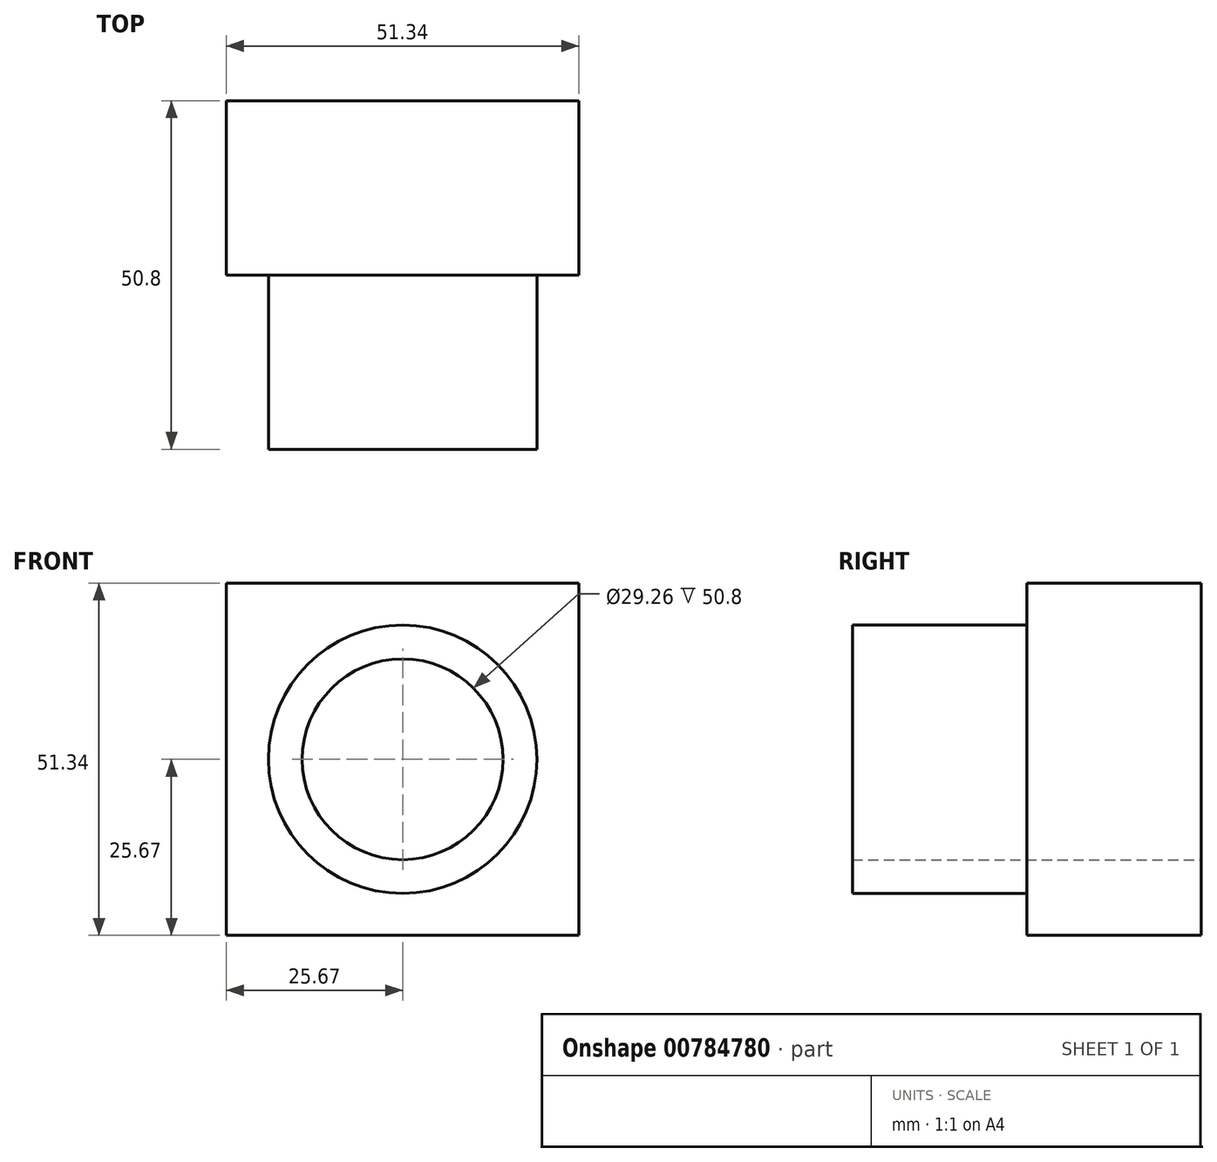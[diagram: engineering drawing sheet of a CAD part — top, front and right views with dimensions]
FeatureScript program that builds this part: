
annotation { "Feature Type Name" : "Feature", "Feature Type Description" : "" }
export const myFeature = defineFeature(function(context is Context, id is Id, definition is map)
    precondition{}
    {
        {
            var Q0;
            Q0=qCreatedBy(makeId("Front.planeOp"),FACE);
            var sketch = newSketch(context, id + "F0", { "sketchPlane" : qUnion([Q0])});
            skLineSegment(sketch, "E0.bottom", {"start": v(-25.67, -25.67) * mm, "end": v(25.67, -25.67) * mm});
            skLineSegment(sketch, "E0.top", {"start": v(-25.67, 25.67) * mm, "end": v(25.67, 25.67) * mm});
            skLineSegment(sketch, "E0.left", {"start": v(-25.67, -25.67) * mm, "end": v(-25.67, 25.67) * mm});
            skLineSegment(sketch, "E0.right", {"start": v(25.67, -25.67) * mm, "end": v(25.67, 25.67) * mm});
            skCircle(sketch, "E1", {"center": v(0, 0) * mm, "radius": 19.56 * mm});
            skCircle(sketch, "E2", {"center": v(0, 0) * mm, "radius": 14.63 * mm});
            skSolve(sketch);
        }
        {
            var Q0;
            Q0 = qSketchRegion(id + "F0", true);
            extrude(context, id + "F1", {"entities" : qUnion([Q0]), "depth" : 25.4 * mm, "offsetDistance" : 25.4 * mm});
        }
        {
            var Q0;
            Q0=makeQuery(id+"F0.imprint","IMPRINT",FACE,{"disambiguationData":[TD([[makeQuery(id+"F0.imprint","IMPRINT",EDGE,{"derivedFrom":sQuery(id+"F0.wireOp",EDGE,"E1")}),1.0]])]});
            extrude(context, id + "F2", {"entities" : qUnion([Q0]), "operationType" : NewBodyOperationType.ADD, "depth" : 50.8 * mm, "offsetDistance" : 25.4 * mm});
        }
    });
